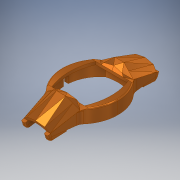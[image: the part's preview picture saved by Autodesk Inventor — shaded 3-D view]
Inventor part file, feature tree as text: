
AUTODESK INVENTOR PART (.ipt)
format: ipt  version: 2019 (Build 230136000, 136)  size: 1,200,128 bytes
history: native  units: mm
features: other x12, sketch x10, projected_geometry x10, plane x7, extrude x6, fillet x4, direct_edit x2, sweep x1, revolve x1, hole x1, mirror x1
ambient origin geometry x8: Origin, YZ Plane, XZ Plane, XY Plane, X Axis, Y Axis, Z Axis, Center Point
bodies: Volumenkörper1 (feature_tree), Volumenkörper2 (feature_tree), Volumenkörper3 (feature_tree), Volumenkörper5 (feature_tree)
feature tree (55):
  other  "Körper verschieben1"
  plane  "Arbeitsebene3"
  other  "Trennen1"
  plane  "Arbeitsebene1"
  sketch  "Skizze2"  dims[d2=90.0deg d3=0.8mm]
  plane  "Arbeitsebene2"
  plane  "Arbeitsebene4"
  other  "Trennen2"
  extrude  "Extrusion3"  Depth=0.8mm
  plane  "Arbeitsebene5"
  sweep  "Sweeping2"
  plane  "Arbeitsebene9"
  other  "Trennen5"
  extrude  "Extrusion4"  Depth=0.8mm TaperAngle=0.0deg
  revolve  "Umdrehung2"
  extrude  "Extrusion5"  Depth=0.45mm
  hole  "Bohrung1"  [1 undecoded]
  other  "Mittelebene"
  plane  "Arbeitsebene7"
  other  "Trennen3"
  mirror  "Spiegeln1"
  other  "Mittelebene_2"
  extrude  "Extrusion6"  Depth=3.5mm TaperAngle=0.0deg
  other  "Kombinieren2"
  fillet  "Rundung1"  Radius=1.745329mm
  fillet  "Rundung2"  Radius=6.0mm
  fillet  "Rundung3"  Radius=2.8mm
  fillet  "Rundung4"  Radius=0.5mm
  extrude  "Extrusion7"  Depth=0.3mm
  direct_edit  "Direktbearbeitung1"
  direct_edit  "Direktbearbeitung2"
  extrude  "Extrusion8"  Depth=1.0mm
  sketch  "Skizze6"  dims[d13=-3.141593mm d14=-3.141593mm]
  projected_geometry  "Projizierte Kontur4"
  sketch  "Skizze7"  dims[d15=0.0mm d16=0.8mm d17=0.0mm]
  sketch  "Skizze8"  dims[d20=0.0mm d21=0.0mm d22=0.45mm]
  sketch  "Skizze9"  dims[d24=0.45mm d25=1.1mm]
  projected_geometry  "Projizierte Kontur6"
  sketch  "Skizze10"  dims[d26=1.1mm d27=3.5mm d28=0.0mm d29=1.745329mm d30=6.0mm d31=0.0mm]
  projected_geometry  "Projizierte Kontur7"
  projected_geometry  "Projizierte Kontur8"
  sketch  "Skizze11"  dims[d32=1.0mm d33=6.0mm d34=4.0mm d35=2.0mm d36=90.0deg d37=8.0mm d38=20.594885mm d40=2.8mm d41=0.5mm d42=0.0mm]
  projected_geometry  "Projizierte Kontur9"
  sketch  "Skizze13"  dims[d43=2.8mm d44=0.3mm]
  projected_geometry  "Projizierte Kontur13"
  projected_geometry  "Projizierte Kontur14"
  projected_geometry  "Projizierte Kontur15"
  sketch  "Skizze14"  dims[d45=2.5mm d46=1.0mm]
  sketch  "Skizze15"  dims[d47=0.3mm d48=0.0mm d49=1.0mm d50=0.0mm d51=10.769mm d52=10.0mm d53=10.0mm d54=10.606061mm d55=10.0mm d56=10.0mm d57=0.3mm d58=0.0mm]
  projected_geometry  "Projizierte Kontur17"
  projected_geometry  "Projizierte Kontur18"
  other  "brep_1"
  other  "Volumenkörper1:1"
  other  "Skalierung1"
  other  "Skalierung2"
note: 1 required parameter value undecoded (feature->parameter linkage not recoverable at this tier; creation-order binding heuristic only, values carry confidence <= 0.55)
